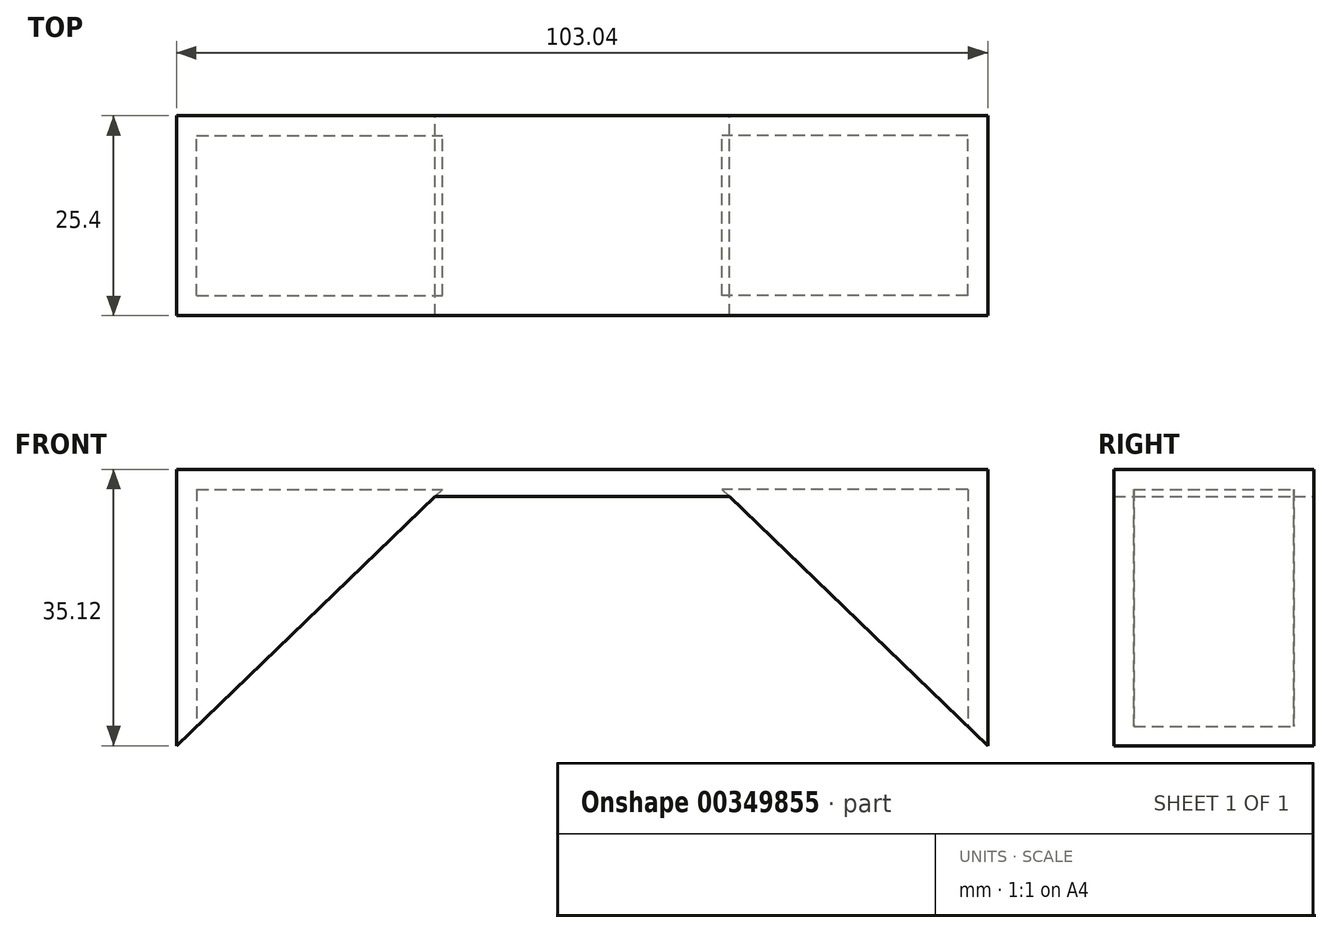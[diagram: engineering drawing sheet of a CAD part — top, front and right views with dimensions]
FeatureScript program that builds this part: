
annotation { "Feature Type Name" : "Feature", "Feature Type Description" : "" }
export const myFeature = defineFeature(function(context is Context, id is Id, definition is map)
    precondition{}
    {
        {
            var Q0;
            Q0=qCreatedBy(makeId("Front.planeOp"),FACE);
            var sketch = newSketch(context, id + "F0", { "sketchPlane" : qUnion([Q0])});
            skLineSegment(sketch, "E0", {"start": v(-51.52, 25.33) * mm, "end": v(0, 25.33) * mm});
            skLineSegment(sketch, "E1", {"start": v(-51.52, 25.33) * mm, "end": v(-51.52, 21.87) * mm});
            skLineSegment(sketch, "E2", {"start": v(-51.52, 21.87) * mm, "end": v(0, 21.87) * mm});
            skLineSegment(sketch, "E3", {"start": v(0, 21.87) * mm, "end": v(0, 25.33) * mm});
            skLineSegment(sketch, "E4", {"start": v(-51.52, 21.87) * mm, "end": v(-51.52, -9.79) * mm});
            skLineSegment(sketch, "E5", {"start": v(-51.52, -9.79) * mm, "end": v(-18.7, 21.87) * mm});
            skSolve(sketch);
        }
        {
            var Q0;
            Q0=makeQuery(id+"F0.imprint","IMPRINT",FACE,{"disambiguationData":[TD([[makeQuery(id+"F0.imprint","IMPRINT",EDGE,{"derivedFrom":sQuery(id+"F0.wireOp",EDGE,"E0")}),-1.0]])]});
            extrude(context, id + "F1", {"entities" : qUnion([Q0]), "depth" : 25.4 * mm});
        }
        {
            var Q0;
            Q0 = qSketchRegion(id + "F0", true);
            extrude(context, id + "F2", {"entities" : qUnion([Q0]), "operationType" : NewBodyOperationType.ADD, "depth" : 25.4 * mm});
        }
        {
            var Q0;
            Q0=makeQuery(id+"F2.opExtrude","SWEPT_FACE",FACE,{"disambiguationData":[OSD([sQuery(id+"F0.wireOp",EDGE,"E5")])]});
            shell(context, id + "F3", {"entities" : qUnion([Q0]), "thickness" : 2.54 * mm});
        }
        {
            var Q0;
            Q0=makeQuery(id+"F1.opExtrude","SWEPT_BODY",BODY,{"disambiguationData":[OSD([sQuery(id+"F0.wireOp",EDGE,"E0"),sQuery(id+"F0.wireOp",EDGE,"E1"),sQuery(id+"F0.wireOp",EDGE,"E2"),sQuery(id+"F0.wireOp",EDGE,"E3")])]});
            var Q1;
            Q1=makeQuery(id+"F1.opExtrude","SWEPT_FACE",FACE,{"disambiguationData":[OSD([sQuery(id+"F0.wireOp",EDGE,"E3")])]});
            mirror(context, id + "F4", {"operationType" : NewBodyOperationType.ADD, "entities" : qUnion([Q0]), "mirrorPlane" : qUnion([Q1])});
        }
    });
